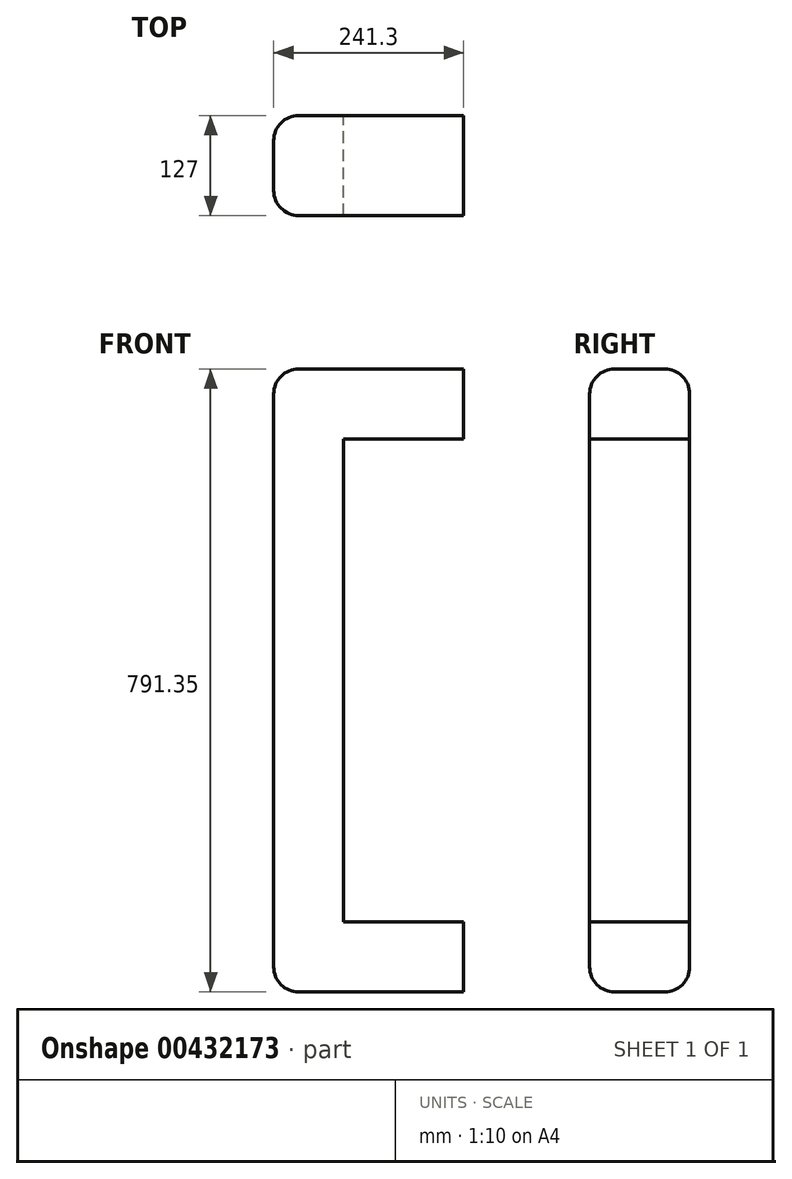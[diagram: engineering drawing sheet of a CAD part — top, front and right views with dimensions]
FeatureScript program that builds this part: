
annotation { "Feature Type Name" : "Feature", "Feature Type Description" : "" }
export const myFeature = defineFeature(function(context is Context, id is Id, definition is map)
    precondition{}
    {
        {
            var Q0;
            Q0=qCreatedBy(makeId("Front.planeOp"),FACE);
            var sketch = newSketch(context, id + "F0", { "sketchPlane" : qUnion([Q0])});
            skLineSegment(sketch, "E0", {"start": v(0, 0) * mm, "end": v(-241.3, 0) * mm});
            skLineSegment(sketch, "E1", {"start": v(-241.3, 0) * mm, "end": v(-241.3, -791.35) * mm});
            skLineSegment(sketch, "E2", {"start": v(-241.3, -791.35) * mm, "end": v(0, -791.35) * mm});
            skLineSegment(sketch, "E3", {"start": v(0, -791.35) * mm, "end": v(0, -702.45) * mm});
            skLineSegment(sketch, "E4", {"start": v(0, -702.45) * mm, "end": v(-152.4, -702.45) * mm});
            skLineSegment(sketch, "E5", {"start": v(-152.4, -702.45) * mm, "end": v(-152.4, -88.9) * mm});
            skLineSegment(sketch, "E6", {"start": v(-152.4, -88.9) * mm, "end": v(0, -88.9) * mm});
            skLineSegment(sketch, "E7", {"start": v(0, -88.9) * mm, "end": v(0, 0) * mm});
            skSolve(sketch);
        }
        {
            var Q0;
            Q0=makeQuery(id+"F0.imprint","IMPRINT",FACE,{"disambiguationData":[TD([[makeQuery(id+"F0.imprint","IMPRINT",EDGE,{"derivedFrom":sQuery(id+"F0.wireOp",EDGE,"E0")}),1.0]])]});
            extrude(context, id + "F1", {"entities" : qUnion([Q0]), "depth" : 127 * mm});
        }
        {
            var Q0;
            Q0=makeQuery(id+"F1.opExtrude","CAP_EDGE",EDGE,{"disambiguationData":[OSD([sQuery(id+"F0.wireOp",EDGE,"E0")])],"isStart":false});
            var Q1;
            Q1=makeQuery(id+"F1.opExtrude","CAP_EDGE",EDGE,{"disambiguationData":[OSD([sQuery(id+"F0.wireOp",EDGE,"E1")])],"isStart":false});
            var Q2;
            Q2=makeQuery(id+"F1.opExtrude","CAP_EDGE",EDGE,{"disambiguationData":[OSD([sQuery(id+"F0.wireOp",EDGE,"E1")])],"isStart":true});
            var Q3;
            Q3=makeQuery(id+"F1.opExtrude","CAP_EDGE",EDGE,{"disambiguationData":[OSD([sQuery(id+"F0.wireOp",EDGE,"E0")])],"isStart":true});
            var Q4;
            Q4=makeQuery(id+"F1.opExtrude","CAP_EDGE",EDGE,{"disambiguationData":[OSD([sQuery(id+"F0.wireOp",EDGE,"E2")])],"isStart":false});
            var Q5;
            Q5=makeQuery(id+"F1.opExtrude","SWEPT_EDGE",EDGE,{"disambiguationData":[OSD([sQuery(id+"F0.wireOp",EDGE,"E1"),sQuery(id+"F0.wireOp",EDGE,"E2")])]});
            var Q6;
            Q6=makeQuery(id+"F1.opExtrude","SWEPT_EDGE",EDGE,{"disambiguationData":[OSD([sQuery(id+"F0.wireOp",EDGE,"E0"),sQuery(id+"F0.wireOp",EDGE,"E1")])]});
            var Q7;
            Q7=makeQuery(id+"F1.opExtrude","CAP_EDGE",EDGE,{"disambiguationData":[OSD([sQuery(id+"F0.wireOp",EDGE,"E2")])],"isStart":true});
            fillet(context, id + "F2", {"entities" : qUnion([Q0, Q1, Q2, Q3, Q4, Q5, Q6, Q7]), "radius" : 31.75 * mm, "tangentPropagation" : true, "allowEdgeOverflow" : false});
        }
    });
